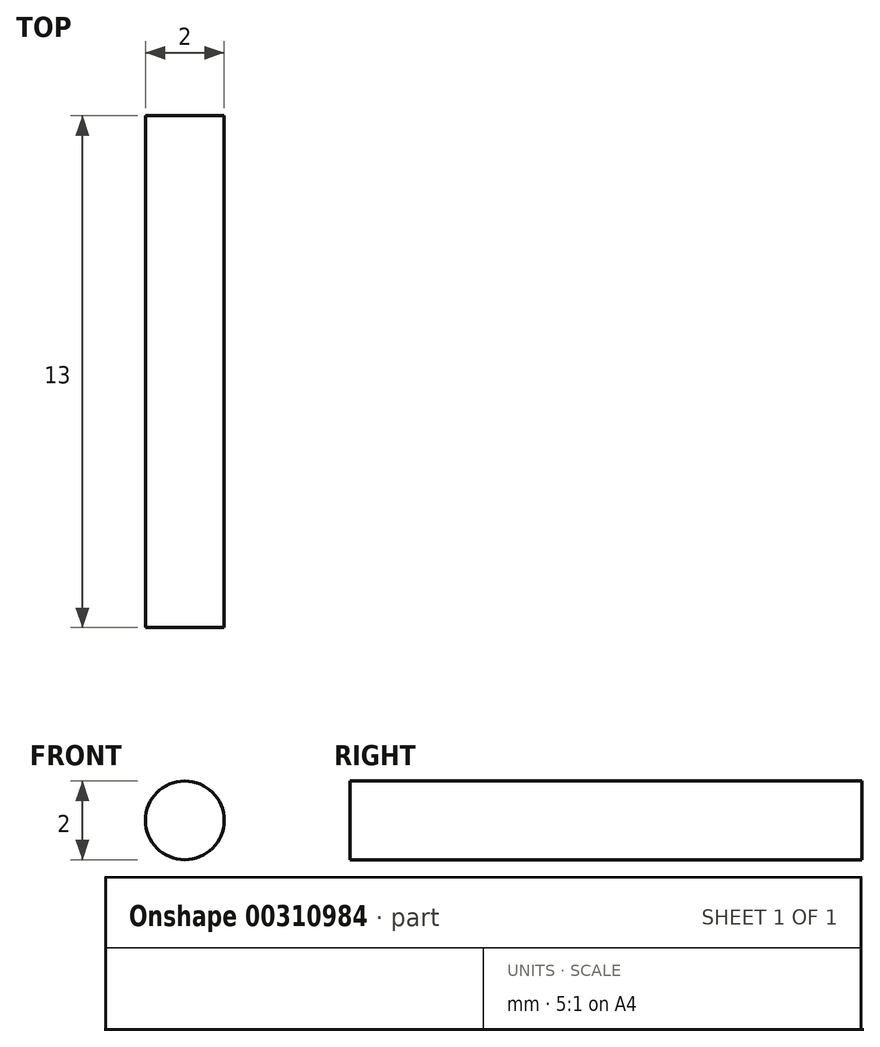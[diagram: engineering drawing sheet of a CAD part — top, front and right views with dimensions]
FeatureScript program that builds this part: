
annotation { "Feature Type Name" : "Feature", "Feature Type Description" : "" }
export const myFeature = defineFeature(function(context is Context, id is Id, definition is map)
    precondition{}
    {
        {
            var Q0;
            Q0=qCreatedBy(makeId("Front.planeOp"),FACE);
            var sketch = newSketch(context, id + "F0", { "sketchPlane" : qUnion([Q0])});
            skCircle(sketch, "E0", {"center": v(0, 0) * mm, "radius": 1 * mm});
            skSolve(sketch);
        }
        {
            var Q0;
            Q0=makeQuery(id+"F0.imprint","IMPRINT",FACE,{"disambiguationData":[TD([[makeQuery(id+"F0.imprint","IMPRINT",EDGE,{"derivedFrom":sQuery(id+"F0.wireOp",EDGE,"E0")}),1.0]])]});
            extrude(context, id + "F1", {"entities" : qUnion([Q0]), "depth" : 13 * mm});
        }
    });
